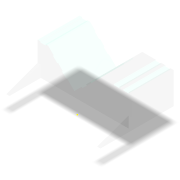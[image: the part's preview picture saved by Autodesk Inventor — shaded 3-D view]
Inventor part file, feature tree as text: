
AUTODESK INVENTOR PART (.ipt)
format: ipt  version: 2022 (Build 260153000, 153)  size: 175,616 bytes
history: native  units: mm
features: sketch x5, extrude x4, projected_geometry x3
ambient origin geometry x8: Origin, YZ Plane, XZ Plane, XY Plane, X Axis, Y Axis, Z Axis, Center Point
bodies: Solid1 (feature_tree)
feature tree (12):
  extrude  "Extrusion1"  Depth=150.0mm
  sketch  "Sketch2"  dims[d2=150.0mm d3=170.0mm]
  extrude  "Extrusion2"  Depth=150.0mm
  extrude  "Extrusion3"  Depth=200.0mm TaperAngle=0.0deg
  extrude  "Extrusion4"  Depth=15.0mm TaperAngle=0.0deg
  sketch  "Sketch1"  dims[d0=340.0mm d1=150.0mm]
  sketch  "Sketch3"  dims[d5=100.0mm d6=200.0mm d7=0.0mm]
  projected_geometry  "Projected Loop1"
  sketch  "Sketch4"  dims[d8=15.0mm d9=0.0mm d10=15.0mm d11=0.0mm]
  projected_geometry  "Projected Loop2"
  sketch  "Sketch5"  dims[d12=3.490659mm d13=150.0mm d16=90.0deg d17=50.0mm d18=50.0mm d19=5.0mm d20=30.0mm d21=5.0mm d22=30.0mm d23=50.0mm d24=30.0mm d25=10.0mm d26=0.0mm d27=5.0mm d28=25.0mm d29=25.0mm d30=20.0mm d31=15.0mm d32=25.0mm d33=12.5mm d34=5.0mm]
  projected_geometry  "Projected Loop3"
